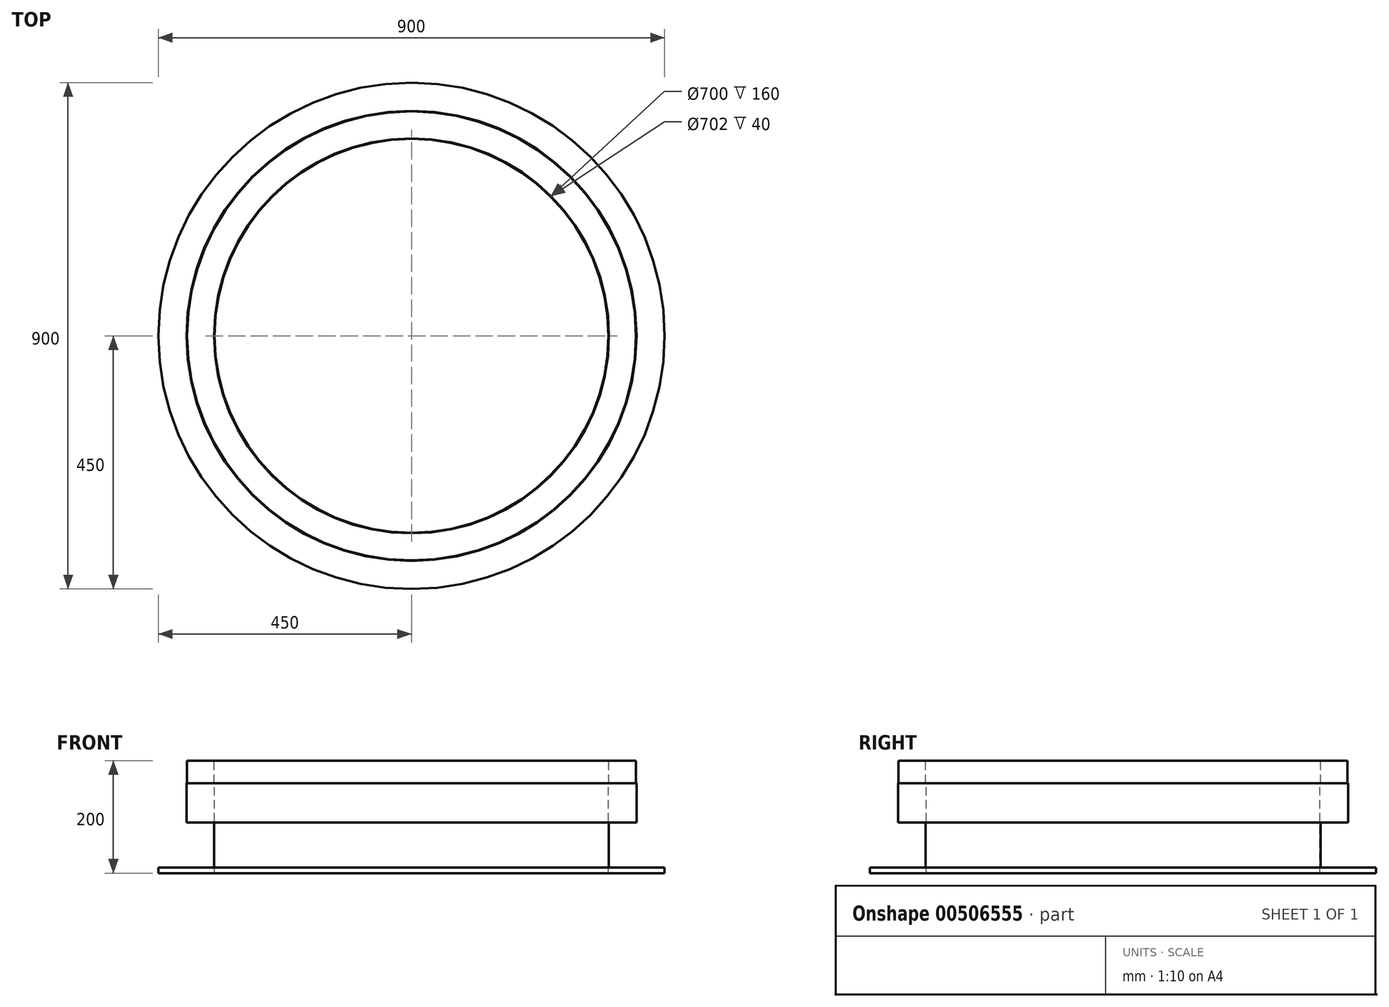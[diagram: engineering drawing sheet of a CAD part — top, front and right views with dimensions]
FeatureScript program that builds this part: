
annotation { "Feature Type Name" : "Feature", "Feature Type Description" : "" }
export const myFeature = defineFeature(function(context is Context, id is Id, definition is map)
    precondition{}
    {
        {
            var Q0;
            Q0=qCreatedBy(makeId("Front.planeOp"),FACE);
            var sketch = newSketch(context, id + "F0", { "sketchPlane" : qUnion([Q0])});
            skLineSegment(sketch, "E0", {"start": v(0, 710.75) * mm, "end": v(0, -704.58) * mm, "construction": true});
            skLineSegment(sketch, "E1", {"start": v(-350, 300.65) * mm, "end": v(-350, 460.65) * mm});
            skLineSegment(sketch, "E2", {"start": v(-350, 460.65) * mm, "end": v(-351, 460.65) * mm});
            skLineSegment(sketch, "E3", {"start": v(-351, 460.65) * mm, "end": v(-351, 500.65) * mm});
            skLineSegment(sketch, "E4", {"start": v(-351, 500.65) * mm, "end": v(-399, 500.65) * mm});
            skLineSegment(sketch, "E5", {"start": v(-399, 500.65) * mm, "end": v(-399, 460.65) * mm});
            skLineSegment(sketch, "E6", {"start": v(-399, 460.65) * mm, "end": v(-400, 460.65) * mm});
            skLineSegment(sketch, "E7", {"start": v(-400, 460.65) * mm, "end": v(-400, 390.65) * mm});
            skLineSegment(sketch, "E8", {"start": v(-400, 390.65) * mm, "end": v(-351, 390.65) * mm});
            skLineSegment(sketch, "E9", {"start": v(-351, 390.65) * mm, "end": v(-351, 310.65) * mm});
            skLineSegment(sketch, "E10", {"start": v(-351, 310.65) * mm, "end": v(-450, 310.65) * mm});
            skLineSegment(sketch, "E11", {"start": v(-450, 310.65) * mm, "end": v(-450, 300.65) * mm});
            skLineSegment(sketch, "E12", {"start": v(-450, 300.65) * mm, "end": v(-350, 300.65) * mm});
            skSolve(sketch);
        }
        {
            var Q0;
            Q0=qSketchRegion(id+"F0",true);
            var Q1;
            Q1=sQuery(id+"F0.wireOp",EDGE,"E0");
            revolve(context, id + "F1", {"entities" : qUnion([Q0]), "axis" : qUnion([Q1]), "revolveType" : RevolveType.FULL});
        }
    });
